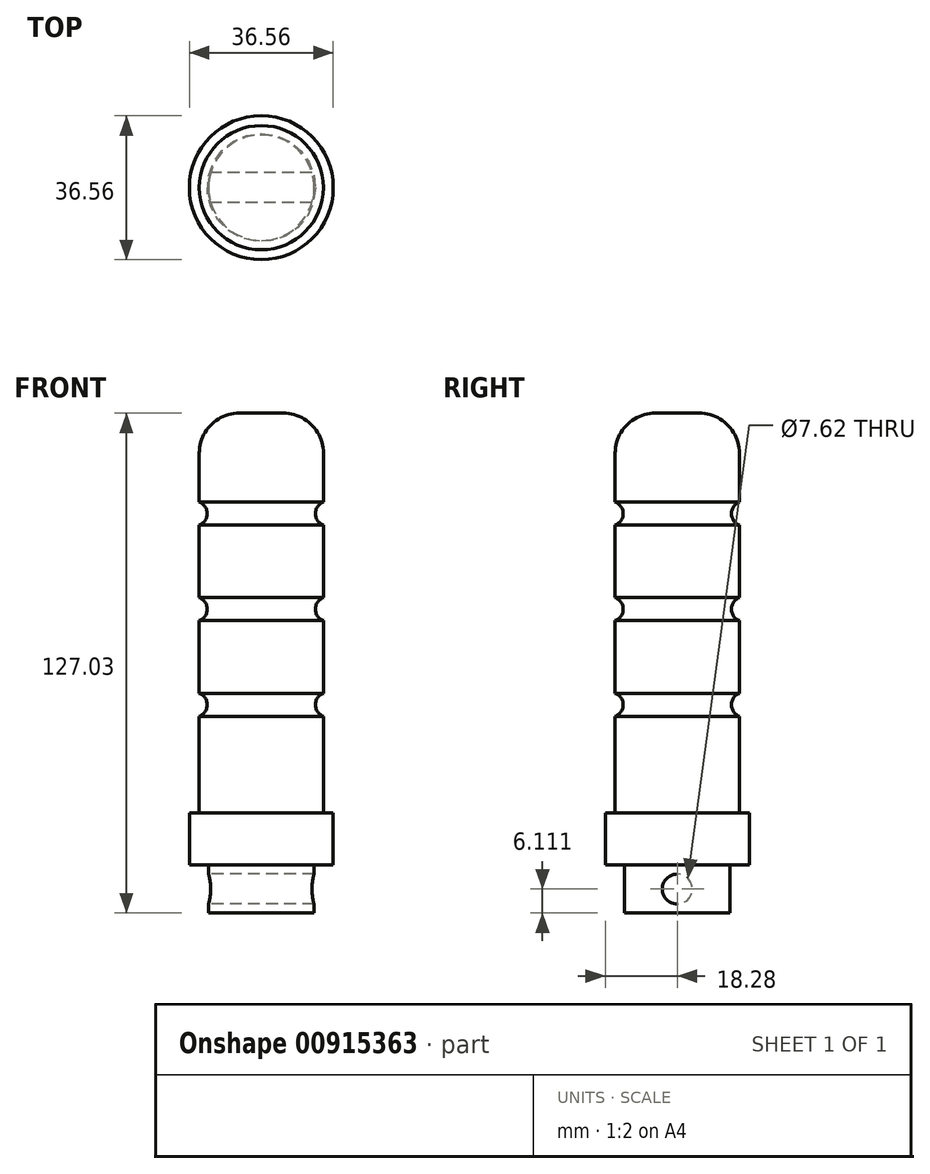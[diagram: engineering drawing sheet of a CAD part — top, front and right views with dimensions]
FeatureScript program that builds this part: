
annotation { "Feature Type Name" : "Feature", "Feature Type Description" : "" }
export const myFeature = defineFeature(function(context is Context, id is Id, definition is map)
    precondition{}
    {
        {
            var Q0;
            Q0=qCreatedBy(makeId("Top.planeOp"),FACE);
            var sketch = newSketch(context, id + "F0", { "sketchPlane" : qUnion([Q0])});
            skCircle(sketch, "E0", {"center": v(0, 0) * mm, "radius": 13.41 * mm});
            skCircle(sketch, "E1", {"center": v(0, 0) * mm, "radius": 18.28 * mm});
            skCircle(sketch, "E2", {"center": v(0, 0) * mm, "radius": 15.77 * mm});
            skSolve(sketch);
        }
        {
            var Q0;
            Q0=makeQuery(id+"F0.imprint","IMPRINT",FACE,{"disambiguationData":[TD([[makeQuery(id+"F0.imprint","IMPRINT",EDGE,{"derivedFrom":sQuery(id+"F0.wireOp",EDGE,"E0")}),1.0]])]});
            extrude(context, id + "F1", {"entities" : qUnion([Q0]), "oppositeDirection" : true, "depth" : 12.22 * mm, "offsetDistance" : 25.4 * mm});
        }
        {
            var Q0;
            Q0=makeQuery(id+"F0.imprint","IMPRINT",FACE,{"disambiguationData":[TD([[makeQuery(id+"F0.imprint","IMPRINT",EDGE,{"derivedFrom":sQuery(id+"F0.wireOp",EDGE,"E0")}),-1.0]])]});
            var Q1;
            Q1=makeQuery(id+"F0.imprint","IMPRINT",FACE,{"disambiguationData":[TD([[makeQuery(id+"F0.imprint","IMPRINT",EDGE,{"derivedFrom":sQuery(id+"F0.wireOp",EDGE,"E0")}),1.0]])]});
            var Q2;
            Q2=sQuery(id+"F0.wireOp",EDGE,"E0");
            var Q3;
            Q3=sQuery(id+"F0.wireOp",EDGE,"E2");
            extrude(context, id + "F2", {"entities" : qUnion([Q0, Q1]), "operationType" : NewBodyOperationType.ADD, "surfaceEntities" : qUnion([Q2, Q3]), "depth" : 114.8 * mm, "offsetDistance" : 25.4 * mm});
        }
        {
            var Q0;
            Q0=makeQuery(id+"F0.imprint","IMPRINT",FACE,{"disambiguationData":[TD([[makeQuery(id+"F0.imprint","IMPRINT",EDGE,{"derivedFrom":sQuery(id+"F0.wireOp",EDGE,"E1")}),1.0]])]});
            var Q1;
            Q1=sQuery(id+"F0.wireOp",EDGE,"E2");
            var Q2;
            Q2=sQuery(id+"F0.wireOp",EDGE,"E1");
            extrude(context, id + "F3", {"entities" : qUnion([Q0]), "operationType" : NewBodyOperationType.ADD, "surfaceEntities" : qUnion([Q1, Q2]), "depth" : 13.2 * mm, "offsetDistance" : 25.4 * mm});
        }
        {
            var Q0;
            Q0=makeQuery(id+"F2.opExtrude","CAP_EDGE",EDGE,{"disambiguationData":[OSD([sQuery(id+"F0.wireOp",EDGE,"E2")])],"isStart":false});
            fillet(context, id + "F4", {"entities" : qUnion([Q0]), "radius" : 10.16 * mm, "tangentPropagation" : true, "allowEdgeOverflow" : false});
        }
        {
            var Q0;
            Q0=qCreatedBy(makeId("Front.planeOp"),FACE);
            var sketch = newSketch(context, id + "F5", { "sketchPlane" : qUnion([Q0])});
            skLineSegment(sketch, "E3", {"start": v(-15.77, 13.2) * mm, "end": v(-15.77, 102.1) * mm});
            skLineSegment(sketch, "E4", {"start": v(15.77, 102.1) * mm, "end": v(15.77, 13.2) * mm});
            skLineSegment(sketch, "E5.0", {"start": v(15.77, 104.65) * mm, "end": v(-15.77, 104.65) * mm});
            skLineSegment(sketch, "E6", {"start": v(0, 114.9) * mm, "end": v(-27.42, 114.9) * mm, "construction": true});
            skLineSegment(sketch, "E7", {"start": v(-27.42, 119.19) * mm, "end": v(-27.42, 0) * mm, "construction": true});
            skLineSegment(sketch, "E8", {"start": v(-24.47, 102.1) * mm, "end": v(-33.43, 102.1) * mm, "construction": true});
            skLineSegment(sketch, "E9", {"start": v(-20.08, 13.2) * mm, "end": v(-32.18, 13.2) * mm, "construction": true});
            skLineSegment(sketch, "E10", {"start": v(-19.5, 37.8) * mm, "end": v(-33.28, 37.8) * mm, "construction": true});
            skLineSegment(sketch, "E11", {"start": v(-19.5, 37.8) * mm, "end": v(-15.77, 37.8) * mm, "construction": true});
            skLineSegment(sketch, "E12", {"start": v(-15.77, 37.8) * mm, "end": v(-15.77, 43.64) * mm});
            skArc(sketch, "E13", {"start": v(-15.77, 37.8) * mm, "mid": v(-13.74, 40.72) * mm, "end": v(-15.77, 43.64) * mm});
            skLineSegment(sketch, "E14", {"start": v(-15.77, 43.64) * mm, "end": v(-15.77, 37.8) * mm});
            skLineSegment(sketch, "E15", {"start": v(0, 0) * mm, "end": v(0, 104.65) * mm, "construction": true});
            skArc(sketch, "E16.0.1.0", {"start": v(-15.77, 62.08) * mm, "mid": v(-13.74, 65) * mm, "end": v(-15.77, 67.92) * mm});
            skArc(sketch, "E16.0.2.0", {"start": v(-15.77, 86.36) * mm, "mid": v(-13.74, 89.28) * mm, "end": v(-15.77, 92.2) * mm});
            skLineSegment(sketch, "E16.direction1", {"start": v(-15.77, 37.8) * mm, "end": v(-41.17, 37.8) * mm, "construction": true});
            skLineSegment(sketch, "E16.direction2", {"start": v(-15.77, 37.8) * mm, "end": v(-15.77, 62.08) * mm, "construction": true});
            skSolve(sketch);
        }
        {
            var Q0;
            Q0=makeQuery(id+"F5.imprint","IMPRINT",FACE,{"disambiguationData":[TD([[makeQuery(id+"F5.imprint","IMPRINT",EDGE,{"derivedFrom":sQuery(id+"F5.wireOp",EDGE,"E13")}),1.0]])]});
            var Q1;
            Q1=sQuery(id+"F5.wireOp",EDGE,"E15");
            revolve(context, id + "F6", {"operationType" : NewBodyOperationType.REMOVE, "surfaceOperationType" : NewSurfaceOperationType.NEW, "entities" : qUnion([Q0]), "axis" : qUnion([Q1]), "revolveType" : RevolveType.FULL, "oppositeDirection" : true});
        }
        {
            var Q0;
            {var subQ0=sQuery(id+"F5.wireOp",EDGE,"E16.0.2.0");Q0=makeQuery(id+"F5.imprint","IMPRINT",FACE,{"disambiguationData":[TD([[makeQuery(id+"F5.imprint","IMPRINT",EDGE,{"derivedFrom":subQ0}),1.0]])]});}
            var Q1;
            {var subQ0=sQuery(id+"F5.wireOp",EDGE,"E16.0.1.0");Q1=makeQuery(id+"F5.imprint","IMPRINT",FACE,{"disambiguationData":[TD([[makeQuery(id+"F5.imprint","IMPRINT",EDGE,{"derivedFrom":subQ0}),1.0]])]});}
            var Q2;
            Q2=sQuery(id+"F5.wireOp",EDGE,"E15");
            revolve(context, id + "F7", {"operationType" : NewBodyOperationType.REMOVE, "surfaceOperationType" : NewSurfaceOperationType.NEW, "entities" : qUnion([Q0, Q1]), "axis" : qUnion([Q2]), "revolveType" : RevolveType.FULL, "oppositeDirection" : true});
        }
        {
            var Q0;
            Q0=qCreatedBy(makeId("Right.planeOp"),FACE);
            var sketch = newSketch(context, id + "F8", { "sketchPlane" : qUnion([Q0])});
            skLineSegment(sketch, "E17", {"start": v(13.41, 0) * mm, "end": v(13.41, -12.22) * mm});
            skLineSegment(sketch, "E18", {"start": v(-13.41, -12.22) * mm, "end": v(-13.41, 0) * mm});
            skLineSegment(sketch, "E19", {"start": v(13.41, -6.1) * mm, "end": v(-13.41, -6.1) * mm, "construction": true});
            skLineSegment(sketch, "E20", {"start": v(0, -12.21) * mm, "end": v(0, -0.9) * mm, "construction": true});
            skCircle(sketch, "E21", {"center": v(0, -6.1) * mm, "radius": 3.81 * mm});
            skSolve(sketch);
        }
        {
            var Q0;
            Q0=makeQuery(id+"F8.imprint","IMPRINT",FACE,{"disambiguationData":[TD([[makeQuery(id+"F8.imprint","IMPRINT",EDGE,{"derivedFrom":sQuery(id+"F8.wireOp",EDGE,"E21")}),1.0]])]});
            extrude(context, id + "F9", {"entities" : qUnion([Q0]), "operationType" : NewBodyOperationType.REMOVE, "endBound" : BoundingType.SYMMETRIC, "depth" : 50.8 * mm, "offsetDistance" : 25.4 * mm});
        }
    });
